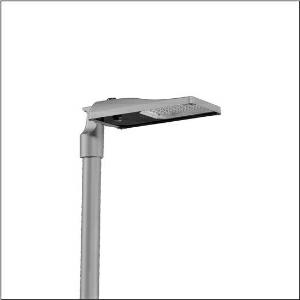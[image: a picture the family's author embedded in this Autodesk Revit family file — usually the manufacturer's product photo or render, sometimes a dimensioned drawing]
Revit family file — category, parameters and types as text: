
# Revit family: streetlight_sl_31_mini___p0_5a_5xh6v31t08ga_58c0
name_source: partatom
category: Lighting Fixtures
units: mm (PartAtom-declared; Revit-internal decimal feet)

## family parameters
Cut with Voids When Loaded = No
Host = Face
Light Source = No
Part Type = Normal
Room Calculation Point = No
Round Connector Dimension = Use Diameter
Shared = No

## types (1)
- --- (1 x LED, 5780 lm, 39.3 W, 3000K)
    Apparent Load = 39 VA
    CIE Flux Codes = 37 73 96 100 100
    Color Rendering = 70
    Color Temperature = 3000K
    Default Elevation = 1800 mm
    Description = Streetlight SL 31 mini D4i, Desk-Remote mast luminaire for post-top, side-entry; light control with lens of PMMA; light distribution: P0.5a, direct asymmetric distribution, for standard-compliant lighting for roads and squares; LED: luminous flux: 5.780lm, light colour: 730, colour temperature: 3000K; luminous efficacy: 147,1lm/W; control: pre-setting: logarithmic dimming characteristic, flexible luminous flux parameterisation, time-dependent luminous flux control, constant luminous flux control, power reduction, intelligent temperature release in ECG and LED module, overheat protection; luminaire housing, of diecast aluminium, SITECO metallic grey (DB 702S), corrosivity category C5 high according to DIN EN ISO 12944; cover of toughened safety glass, transparent, opened without tools; mast flange of diecast aluminium, SITECO metallic grey (DB 702S), spigot size: 76/60mm, mast flange included unmounted; cable length: 6,5m, connection cable pre-assembled; mains connection: 220..240V, AC, 50/60Hz; power consumption (at start of service life): 39,3W / (at end of service life): 40,7W / (with reduced operation 50%): 18,1W; protection rating (complete): IP66; insulation class (complete): insulation class II (safety insulation); impact resistance: IK09; certification: CE, ENEC, ENEC+, VDE, UKCA, ZD4i; permissible operating ambient temperature for outdoor applications: -40..+50°C; packaging unit: 1 piece

Light Distribution: P0.5a
    Height = 76 mm
    Lamp = 1 x LED
    Lamp Light Flux = 5780 lm
    Lamp Power = 39.3 W
    Lamp count = 1
    Length = 547 mm
    Luminous efficacy = 147 lm/W
    Manufacturer = Siteco
    ModVariant = No
    Model = 5XH6V31T08GA
    Number of Poles = 1
    OnlyDefault = Yes
    Power Factor = 1
    Product Name = Streetlight SL 31 mini | P0.5a
    Product group = mast luminaire | pylon top
    ProductGroupID = 6100
    Protection Class = Protection class II
    Protection Degree = IP 66
    RLX_Detail_Level = 1
    RLX_Emergency_Light_Flux = 0 lm
    RLX_Emergency_Type = 0
    RLX_Emergency_Type_DB = No
    RlxData = <blob elided: 39357 chars, md5=6ad1b66f>
    Socket = socket
    Standby Power = 0 W
    System Light Flux = 5780 lm
    System Power = 39 W
    Type Comments = factory setting: luminous flux: 100 % | dim-lin: 254 | 798 mA
    Type Image = l_1300332.jpg
    URL = http://relux.com
    VarID = @adj_065001
    Voltage = 0 V
    Weight = 0.00 kg
    Width = 265 mm

## geometry (parser evidence)
native form markers: Blend x4, Sweep x10
no freeform markers — native parametric forms only
